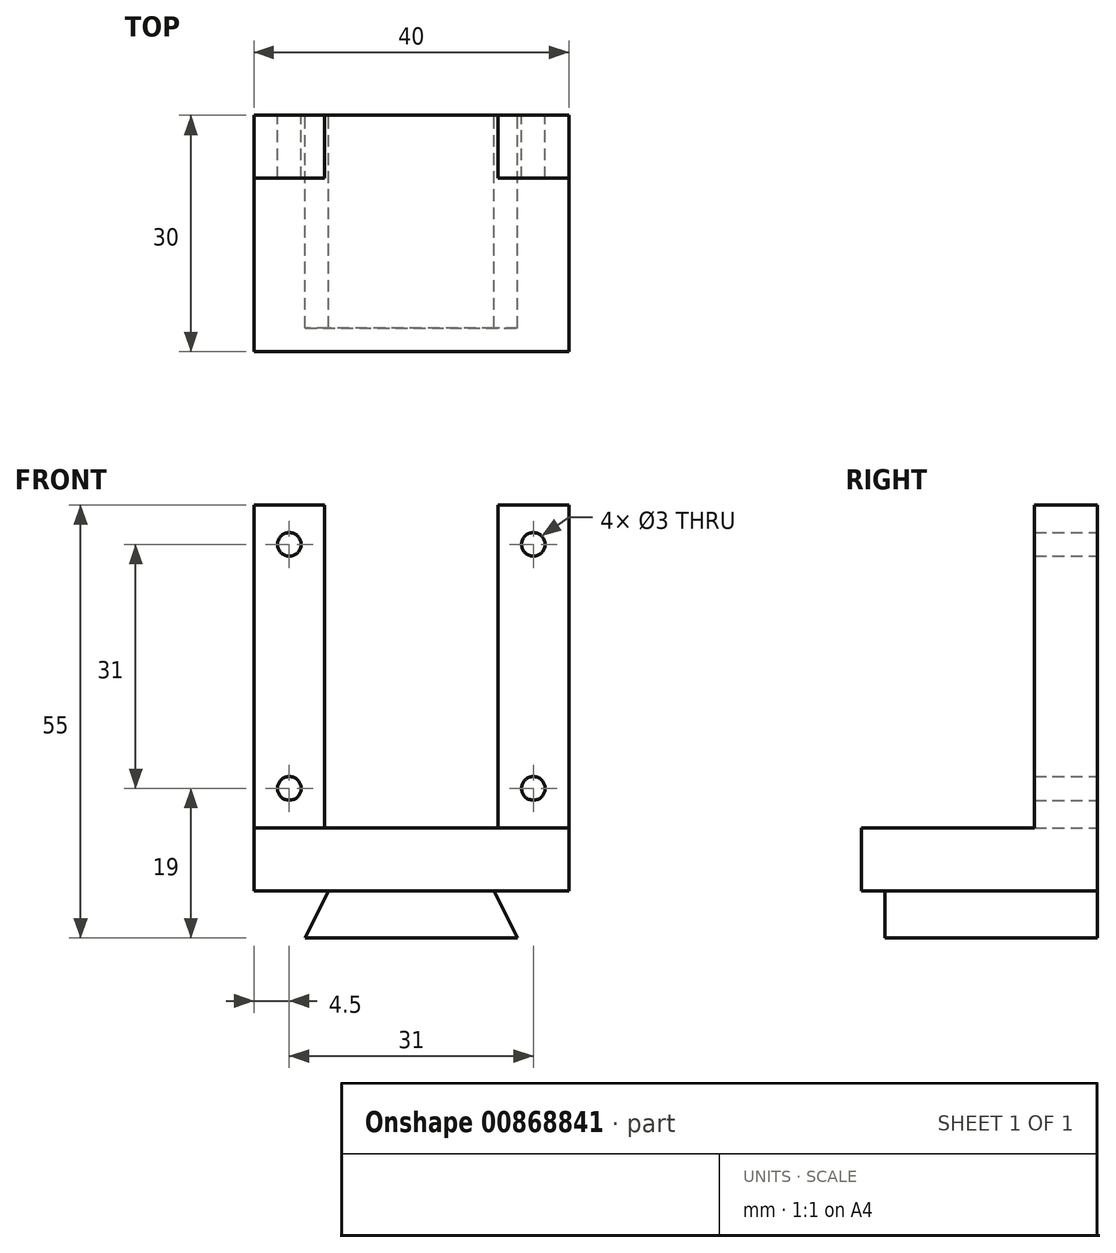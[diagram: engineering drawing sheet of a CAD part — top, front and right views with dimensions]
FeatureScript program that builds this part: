
annotation { "Feature Type Name" : "Feature", "Feature Type Description" : "" }
export const myFeature = defineFeature(function(context is Context, id is Id, definition is map)
    precondition{}
    {
        {
            var Q0;
            Q0=qCreatedBy(makeId("Front.planeOp"),FACE);
            var sketch = newSketch(context, id + "F0", { "sketchPlane" : qUnion([Q0])});
            skLineSegment(sketch, "E0", {"start": v(-13.5, 0) * mm, "end": v(13.5, 0) * mm});
            skLineSegment(sketch, "E1", {"start": v(13.5, 0) * mm, "end": v(10.5, 6) * mm});
            skLineSegment(sketch, "E2", {"start": v(10.5, 6) * mm, "end": v(-10.5, 6) * mm});
            skLineSegment(sketch, "E3", {"start": v(-10.5, 6) * mm, "end": v(-13.5, 0) * mm});
            skSolve(sketch);
        }
        {
            var Q0;
            Q0 = qSketchRegion(id + "F0", true);
            extrude(context, id + "F1", {"entities" : qUnion([Q0]), "depth" : 27 * mm, "offsetDistance" : 25 * mm});
        }
        {
            var Q0;
            Q0=qCreatedBy(makeId("Front.planeOp"),FACE);
            var sketch = newSketch(context, id + "F2", { "sketchPlane" : qUnion([Q0])});
            skLineSegment(sketch, "E4.0", {"start": v(10.5, 6) * mm, "end": v(-10.5, 6) * mm});
            skLineSegment(sketch, "E5", {"start": v(-20, 6) * mm, "end": v(20, 6) * mm});
            skLineSegment(sketch, "E6", {"start": v(20, 6) * mm, "end": v(20, 55) * mm});
            skLineSegment(sketch, "E7", {"start": v(20, 55) * mm, "end": v(11, 55) * mm});
            skLineSegment(sketch, "E8", {"start": v(11, 55) * mm, "end": v(11, 14) * mm});
            skLineSegment(sketch, "E9", {"start": v(11, 14) * mm, "end": v(-11, 14) * mm});
            skLineSegment(sketch, "E10", {"start": v(-11, 14) * mm, "end": v(-11, 55) * mm});
            skLineSegment(sketch, "E11", {"start": v(-11, 55) * mm, "end": v(-20, 55) * mm});
            skLineSegment(sketch, "E12", {"start": v(-20, 55) * mm, "end": v(-20, 6) * mm});
            skPoint(sketch, "E13", {"position": v(0, 14) * mm});
            skPoint(sketch, "E14", {"position": v(0, 6) * mm});
            skCircle(sketch, "E15", {"center": v(-15.5, 50) * mm, "radius": 1.5 * mm});
            skPoint(sketch, "E15.centerSnap0", {"position": v(-15.5, 55) * mm});
            skCircle(sketch, "E16", {"center": v(-15.5, 19) * mm, "radius": 1.5 * mm});
            skCircle(sketch, "E17", {"center": v(15.5, 50) * mm, "radius": 1.5 * mm});
            skPoint(sketch, "E17.centerSnap0", {"position": v(15.5, 55) * mm});
            skCircle(sketch, "E18", {"center": v(15.5, 19) * mm, "radius": 1.5 * mm});
            skSolve(sketch);
        }
        {
            var Q0;
            Q0 = qSketchRegion(id + "F2", true);
            extrude(context, id + "F3", {"entities" : qUnion([Q0]), "operationType" : NewBodyOperationType.ADD, "depth" : 8 * mm, "offsetDistance" : 25 * mm});
        }
        {
            var Q0;
            Q0=qCreatedBy(makeId("Front.planeOp"),FACE);
            var sketch = newSketch(context, id + "F4", { "sketchPlane" : qUnion([Q0])});
            skLineSegment(sketch, "E19.bottom", {"start": v(20, 6) * mm, "end": v(-20, 6) * mm});
            skLineSegment(sketch, "E19.top", {"start": v(20, 14) * mm, "end": v(-20, 14) * mm});
            skLineSegment(sketch, "E19.left", {"start": v(20, 6) * mm, "end": v(20, 14) * mm});
            skLineSegment(sketch, "E19.right", {"start": v(-20, 6) * mm, "end": v(-20, 14) * mm});
            skSolve(sketch);
        }
        {
            var Q0;
            Q0 = qSketchRegion(id + "F4", true);
            extrude(context, id + "F5", {"entities" : qUnion([Q0]), "operationType" : NewBodyOperationType.ADD, "depth" : 30 * mm, "offsetDistance" : 25 * mm});
        }
    });
